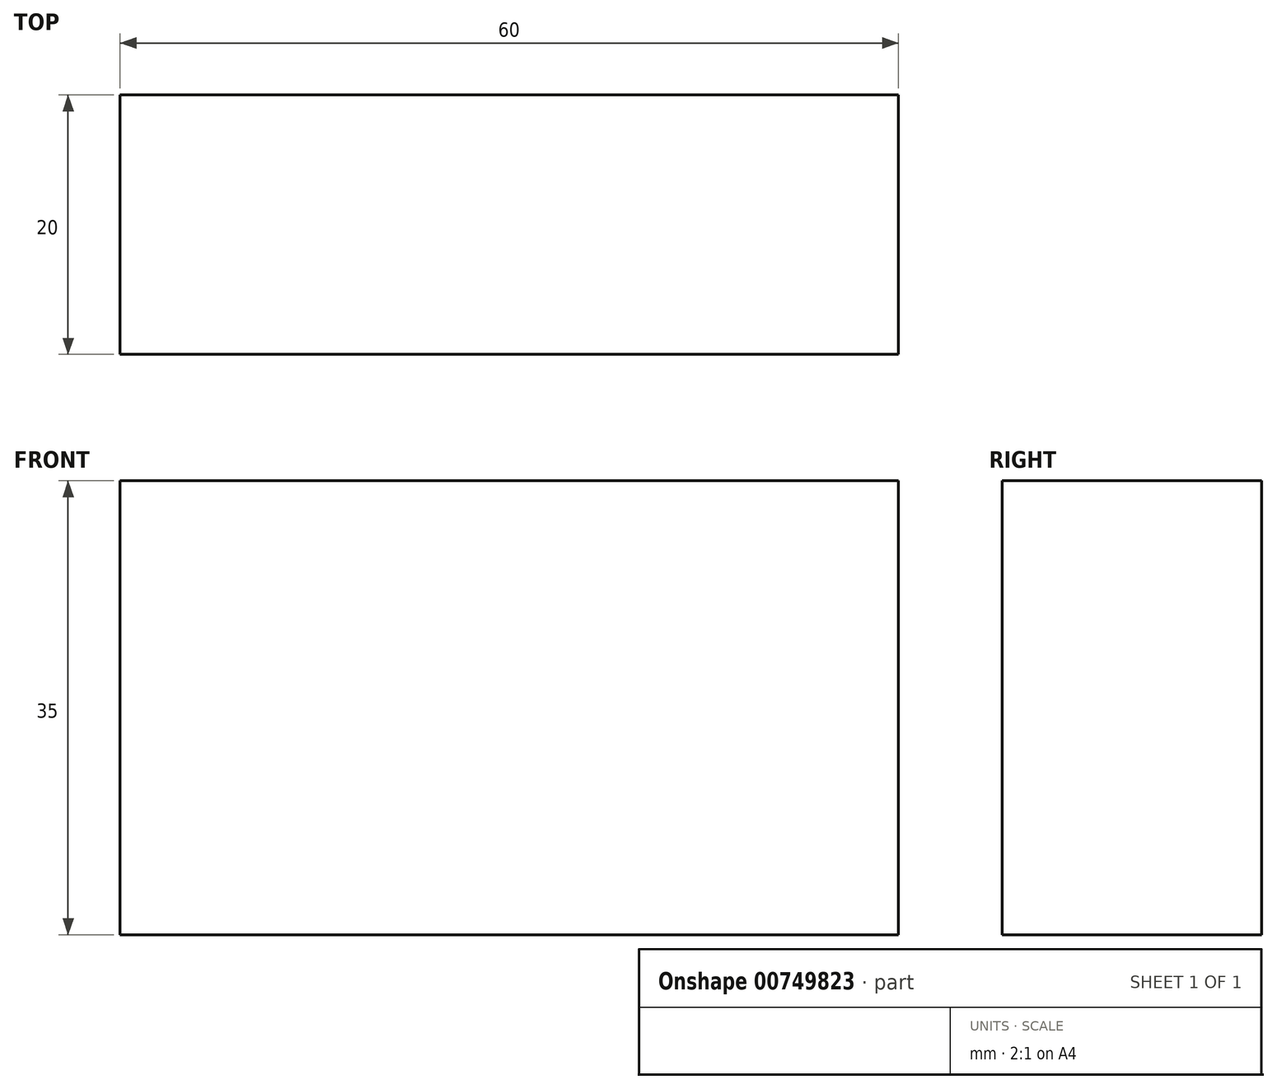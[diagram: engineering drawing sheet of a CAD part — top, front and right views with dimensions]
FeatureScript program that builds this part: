
annotation { "Feature Type Name" : "Feature", "Feature Type Description" : "" }
export const myFeature = defineFeature(function(context is Context, id is Id, definition is map)
    precondition{}
    {
        {
            var Q0;
            Q0=qCreatedBy(makeId("Top.planeOp"),FACE);
            var sketch = newSketch(context, id + "F0", { "sketchPlane" : qUnion([Q0])});
            skLineSegment(sketch, "E0.bottom", {"start": v(0, 0) * mm, "end": v(60, 0) * mm});
            skLineSegment(sketch, "E0.top", {"start": v(0, 20) * mm, "end": v(60, 20) * mm});
            skLineSegment(sketch, "E0.left", {"start": v(0, 0) * mm, "end": v(0, 20) * mm});
            skLineSegment(sketch, "E0.right", {"start": v(60, 0) * mm, "end": v(60, 20) * mm});
            skSolve(sketch);
        }
        {
            var Q0;
            Q0=makeQuery(id+"F0.imprint","IMPRINT",FACE,{"disambiguationData":[TD([[makeQuery(id+"F0.imprint","IMPRINT",EDGE,{"derivedFrom":sQuery(id+"F0.wireOp",EDGE,"E0.bottom")}),1.0]])]});
            extrude(context, id + "F1", {"entities" : qUnion([Q0]), "depth" : 35 * mm, "offsetDistance" : 25 * mm});
        }
    });
